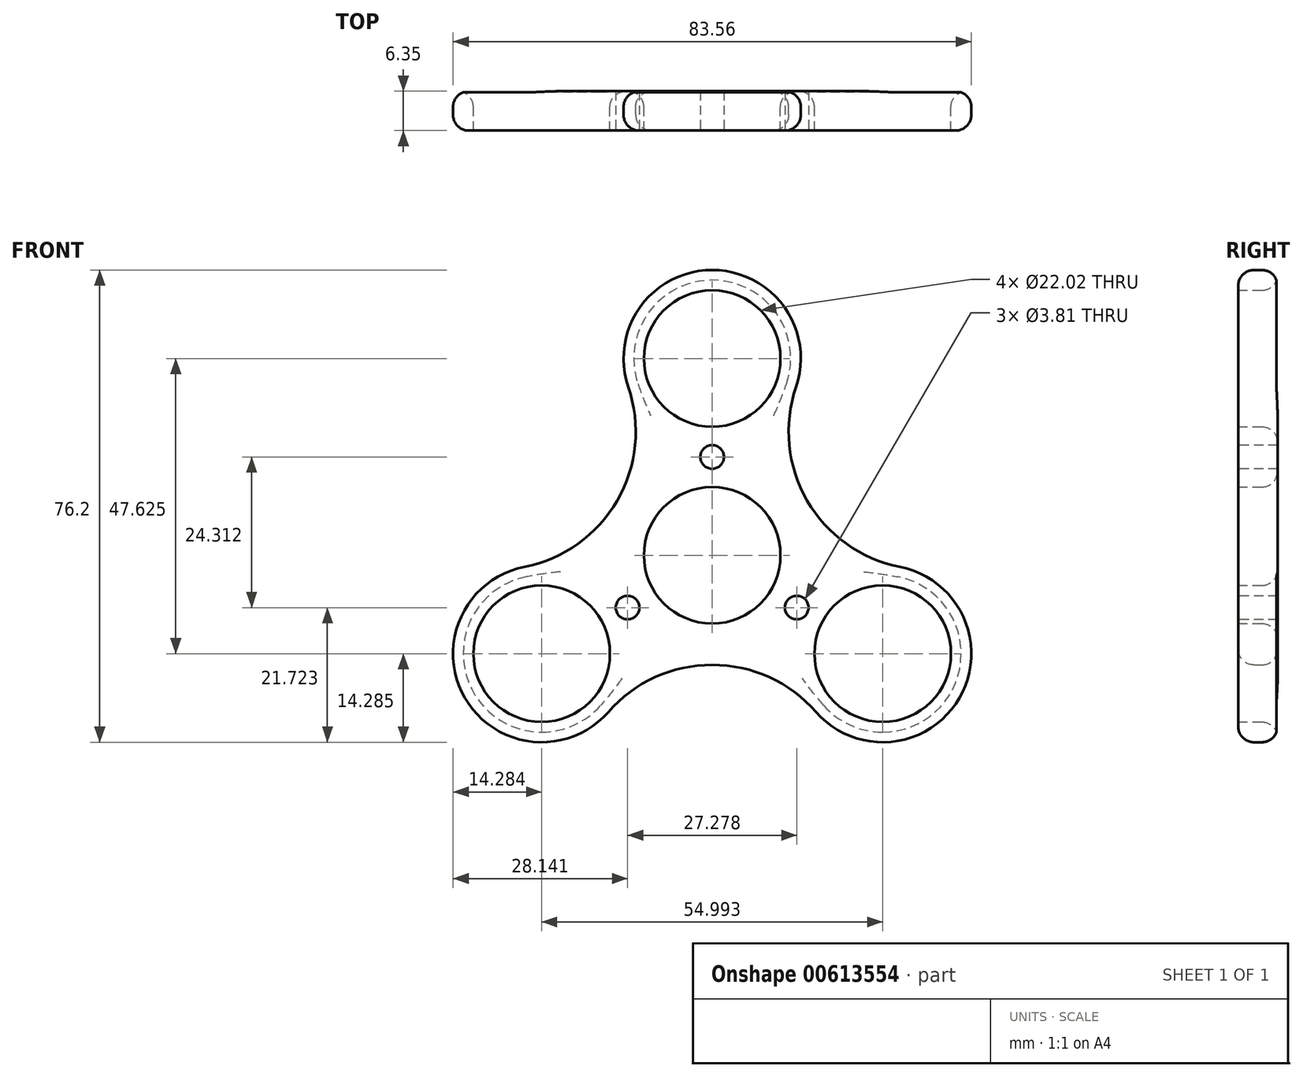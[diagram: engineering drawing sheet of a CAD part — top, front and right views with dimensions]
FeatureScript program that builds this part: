
annotation { "Feature Type Name" : "Feature", "Feature Type Description" : "" }
export const myFeature = defineFeature(function(context is Context, id is Id, definition is map)
    precondition{}
    {
        {
            var Q0;
            Q0=qCreatedBy(makeId("Front.planeOp"),FACE);
            var sketch = newSketch(context, id + "F0", { "sketchPlane" : qUnion([Q0])});
            skCircle(sketch, "E0", {"center": v(0, 0) * mm, "radius": 11.01 * mm});
            skCircle(sketch, "E1", {"center": v(0, 0) * mm, "radius": 14.29 * mm});
            skCircle(sketch, "E2", {"center": v(0, 31.75) * mm, "radius": 11.01 * mm});
            skCircle(sketch, "E3", {"center": v(0, 31.75) * mm, "radius": 14.29 * mm});
            skCircle(sketch, "E4.1.0", {"center": v(-27.5, -15.87) * mm, "radius": 14.29 * mm});
            skCircle(sketch, "E4.2.0", {"center": v(27.5, -15.88) * mm, "radius": 14.29 * mm});
            skCircle(sketch, "E5", {"center": v(-27.5, -15.87) * mm, "radius": 11.01 * mm});
            skCircle(sketch, "E6", {"center": v(27.5, -15.88) * mm, "radius": 11.01 * mm});
            skArc(sketch, "E7", {"start": v(-30.26, -1.86) * mm, "mid": v(-15.3, 8.84) * mm, "end": v(-13.52, 27.13) * mm});
            skArc(sketch, "E8", {"start": v(13.52, 27.13) * mm, "mid": v(15.3, 8.84) * mm, "end": v(30.26, -1.86) * mm});
            skArc(sketch, "E9", {"start": v(16.74, -25.28) * mm, "mid": v(0, -17.67) * mm, "end": v(-16.74, -25.28) * mm});
            skSolve(sketch);
        }
        {
            var Q0;
            Q0=makeQuery(id+"F0.imprint","IMPRINT",FACE,{"disambiguationData":[TD([[makeQuery(id+"F0.imprint","IMPRINT",EDGE,{"derivedFrom":sQuery(id+"F0.wireOp",EDGE,"E1")}),-1.0]])]});
            var Q1;
            Q1=makeQuery(id+"F0.imprint","IMPRINT",FACE,{"disambiguationData":[TD([[makeQuery(id+"F0.imprint","IMPRINT",EDGE,{"derivedFrom":sQuery(id+"F0.wireOp",EDGE,"E5")}),-1.0]])]});
            var Q2;
            Q2=makeQuery(id+"F0.imprint","IMPRINT",FACE,{"disambiguationData":[TD([[makeQuery(id+"F0.imprint","IMPRINT",EDGE,{"derivedFrom":sQuery(id+"F0.wireOp",EDGE,"E0")}),-1.0]])]});
            var Q3;
            Q3=makeQuery(id+"F0.imprint","IMPRINT",FACE,{"disambiguationData":[TD([[makeQuery(id+"F0.imprint","IMPRINT",EDGE,{"derivedFrom":sQuery(id+"F0.wireOp",EDGE,"E6")}),-1.0]])]});
            var Q4;
            Q4=makeQuery(id+"F0.imprint","IMPRINT",FACE,{"disambiguationData":[TD([[makeQuery(id+"F0.imprint","IMPRINT",EDGE,{"derivedFrom":sQuery(id+"F0.wireOp",EDGE,"E2")}),-1.0]])]});
            extrude(context, id + "F1", {"entities" : qUnion([Q0, Q1, Q2, Q3, Q4]), "depth" : 6.35 * mm, "offsetDistance" : 25.4 * mm});
        }
        {
            var Q0;
            Q0=makeQuery(id+"F1.opExtrude","CAP_EDGE",EDGE,{"disambiguationData":[OSD([sQuery(id+"F0.wireOp",EDGE,"E7")])],"isStart":false});
            fillet(context, id + "F2", {"entities" : qUnion([Q0]), "radius" : 2.54 * mm, "tangentPropagation" : true, "allowEdgeOverflow" : false});
        }
        {
            var Q0;
            Q0=makeQuery(id+"F1.opExtrude","CAP_FACE",FACE,{"disambiguationData":[OSD([sQuery(id+"F0.wireOp",EDGE,"E0"),sQuery(id+"F0.wireOp",EDGE,"E2"),sQuery(id+"F0.wireOp",EDGE,"E3"),sQuery(id+"F0.wireOp",EDGE,"E4.1.0"),sQuery(id+"F0.wireOp",EDGE,"E4.2.0"),sQuery(id+"F0.wireOp",EDGE,"E5"),sQuery(id+"F0.wireOp",EDGE,"E6"),sQuery(id+"F0.wireOp",EDGE,"E7"),sQuery(id+"F0.wireOp",EDGE,"E8"),sQuery(id+"F0.wireOp",EDGE,"E9")])],"isStart":true});
            fillet(context, id + "F3", {"entities" : qUnion([Q0]), "radius" : 2.54 * mm, "tangentPropagation" : true, "allowEdgeOverflow" : false});
        }
        {
            var Q0;
            Q0=makeQuery(id+"F1.opExtrude","CAP_FACE",FACE,{"disambiguationData":[OSD([sQuery(id+"F0.wireOp",EDGE,"E0"),sQuery(id+"F0.wireOp",EDGE,"E2"),sQuery(id+"F0.wireOp",EDGE,"E3"),sQuery(id+"F0.wireOp",EDGE,"E4.1.0"),sQuery(id+"F0.wireOp",EDGE,"E4.2.0"),sQuery(id+"F0.wireOp",EDGE,"E5"),sQuery(id+"F0.wireOp",EDGE,"E6"),sQuery(id+"F0.wireOp",EDGE,"E7"),sQuery(id+"F0.wireOp",EDGE,"E8"),sQuery(id+"F0.wireOp",EDGE,"E9")])],"isStart":false});
            var sketch = newSketch(context, id + "F4", { "sketchPlane" : qUnion([Q0])});
            skCircle(sketch, "E10", {"center": v(0, 15.88) * mm, "radius": 1.9 * mm});
            skCircle(sketch, "E11", {"center": v(-13.64, -8.44) * mm, "radius": 1.9 * mm});
            skCircle(sketch, "E12", {"center": v(13.64, -8.44) * mm, "radius": 1.9 * mm});
            skSolve(sketch);
        }
        {
            var Q0;
            Q0=makeQuery(id+"F4.imprint","IMPRINT",FACE,{"disambiguationData":[TD([[makeQuery(id+"F4.imprint","IMPRINT",EDGE,{"derivedFrom":sQuery(id+"F4.wireOp",EDGE,"E11")}),1.0]])]});
            var Q1;
            Q1=makeQuery(id+"F4.imprint","IMPRINT",FACE,{"disambiguationData":[TD([[makeQuery(id+"F4.imprint","IMPRINT",EDGE,{"derivedFrom":sQuery(id+"F4.wireOp",EDGE,"E12")}),1.0]])]});
            var Q2;
            Q2=makeQuery(id+"F4.imprint","IMPRINT",FACE,{"disambiguationData":[TD([[makeQuery(id+"F4.imprint","IMPRINT",EDGE,{"derivedFrom":sQuery(id+"F4.wireOp",EDGE,"E10")}),1.0]])]});
            extrude(context, id + "F5", {"entities" : qUnion([Q0, Q1, Q2]), "operationType" : NewBodyOperationType.REMOVE, "oppositeDirection" : true, "depth" : 25.4 * mm, "offsetDistance" : 25.4 * mm});
        }
    });
